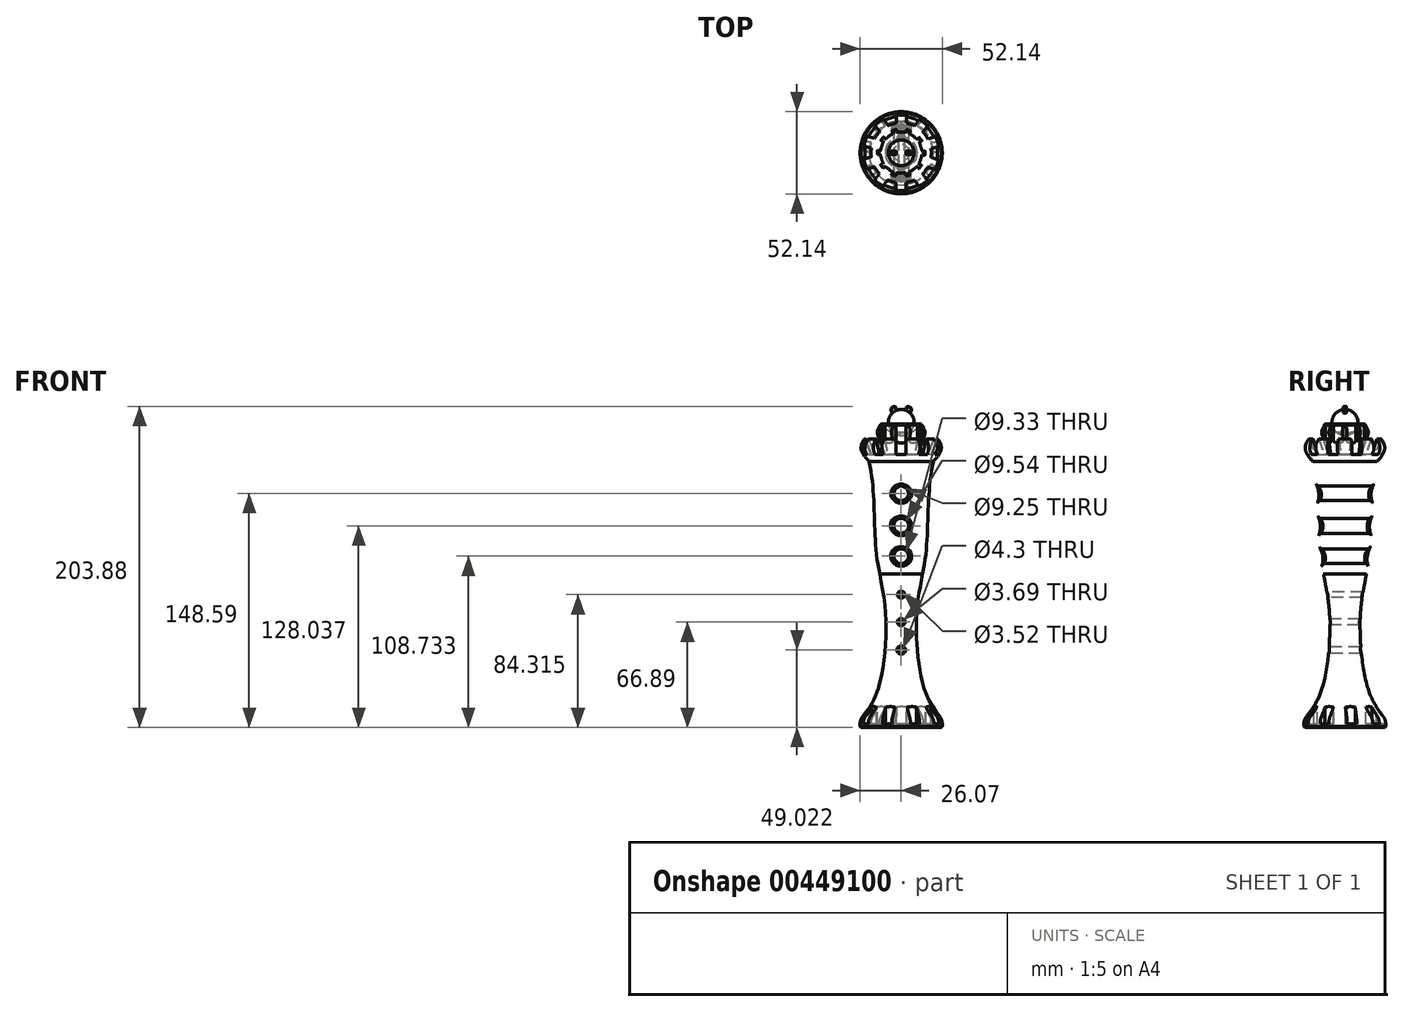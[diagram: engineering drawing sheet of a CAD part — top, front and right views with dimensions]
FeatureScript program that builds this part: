
annotation { "Feature Type Name" : "Feature", "Feature Type Description" : "" }
export const myFeature = defineFeature(function(context is Context, id is Id, definition is map)
    precondition{}
    {
        {
            var Q0;
            Q0=qCreatedBy(makeId("Front.planeOp"),FACE);
            var sketch = newSketch(context, id + "F0", { "sketchPlane" : qUnion([Q0])});
            skLineSegment(sketch, "E0", {"start": v(0, -66.9) * mm, "end": v(-25.47, -66.9) * mm});
            skLineSegment(sketch, "E1", {"start": v(-25.47, -66.9) * mm, "end": v(-26.07, -66.28) * mm});
            skLineSegment(sketch, "E2", {"start": v(-26.07, -66.28) * mm, "end": v(-26.07, -61.96) * mm});
            skFitSpline(sketch, "E3", {"points": [v(-26.07, -61.96) * mm, v(-14.8, -42.88) * mm, v(-9.75, 3.93) * mm, v(-13.6, 30.68) * mm], "startDerivative": vector(46.72, 58.33) * mm, "endDerivative": vector(-14.64, 88.37) * mm});
            skLineSegment(sketch, "E4", {"start": v(0, 71.96) * mm, "end": v(0, -66.9) * mm});
            skFitSpline(sketch, "E5", {"points": [v(-13.6, 30.68) * mm, v(-20.4, 102.06) * mm], "startDerivative": vector(-15.53, 69.23) * mm, "endDerivative": vector(-15.53, 69.23) * mm});
            skLineSegment(sketch, "E6", {"start": v(-20.4, 102.06) * mm, "end": v(0, 102.06) * mm});
            skLineSegment(sketch, "E7", {"start": v(0, 102.06) * mm, "end": v(0, 71.96) * mm});
            skFitSpline(sketch, "E8", {"points": [v(-20.4, 102.06) * mm, v(-23.45, 105.65) * mm, v(-25.43, 109.97) * mm, v(-23.1, 116.39) * mm], "startDerivative": vector(-17.16, 17.67) * mm, "endDerivative": vector(13.07, 17.45) * mm});
            skLineSegment(sketch, "E9", {"start": v(-23.1, 116.39) * mm, "end": v(-19.12, 106.54) * mm});
            skLineSegment(sketch, "E10", {"start": v(-19.12, 106.54) * mm, "end": v(0, 106.54) * mm});
            skLineSegment(sketch, "E11", {"start": v(0, 106.54) * mm, "end": v(0, 102.06) * mm});
            skLineSegment(sketch, "E12", {"start": v(0, 126.8) * mm, "end": v(0, 106.54) * mm});
            skLineSegment(sketch, "E13.MirrorCS", {"start": v(9.8, 106.54) * mm, "end": v(0, 106.54) * mm});
            skPoint(sketch, "E14.orphan", {"position": v(19.12, 106.54) * mm});
            skPoint(sketch, "E15", {"position": v(-3.48, 106.54) * mm});
            skFitSpline(sketch, "E16", {"points": [v(-10.2, 106.54) * mm, v(-14.51, 117.77) * mm, v(-15, 121.47) * mm, v(-13.02, 125.3) * mm], "startDerivative": vector(-11.04, 27.47) * mm, "endDerivative": vector(9.28, 14.07) * mm});
            skFitSpline(sketch, "E17", {"points": [v(-13.02, 125.3) * mm, v(-12.3, 125.9) * mm, v(-9.15, 122.08) * mm, v(0, 120.1) * mm], "startDerivative": vector(4.28, 6.55) * mm, "endDerivative": vector(21.3, -0.4) * mm});
            skLineSegment(sketch, "E18", {"start": v(0, 120.1) * mm, "end": v(0, 106.54) * mm});
            skCircle(sketch, "E19", {"center": v(0, 126.8) * mm, "radius": 8.23 * mm});
            skLineSegment(sketch, "E20", {"start": v(0, 137.4) * mm, "end": v(0, 116.67) * mm});
            skSolve(sketch);
        }
        {
            var Q0;
            {var subQ3=sQuery(id+"F0.wireOp",EDGE,"E0");Q0=makeQuery(id+"F0.imprint","IMPRINT",FACE,{"disambiguationData":[TD([[makeQuery(id+"F0.imprint","IMPRINT",EDGE,{"derivedFrom":subQ3}),-1.0]])]});}
            var Q1;
            Q1=makeQuery(id+"F0.imprint","IMPRINT",FACE,{"disambiguationData":[TD([[makeQuery(id+"F0.imprint","IMPRINT",EDGE,{"derivedFrom":sQuery(id+"F0.wireOp",EDGE,"E6")}),1.0]])]});
            var Q2;
            {var subQ2=sQuery(id+"F0.wireOp",EDGE,"E16");Q2=makeQuery(id+"F0.imprint","IMPRINT",FACE,{"disambiguationData":[TD([[makeQuery(id+"F0.imprint","IMPRINT",EDGE,{"derivedFrom":subQ2}),-1.0]])]});}
            var Q3;
            Q3=sQuery(id+"F0.wireOp",EDGE,"E4");
            revolve(context, id + "F1", {"entities" : qUnion([Q0, Q1, Q2]), "axis" : qUnion([Q3]), "revolveType" : RevolveType.FULL});
        }
        {
            var Q0;
            Q0=qCreatedBy(makeId("Top.planeOp"),FACE);
            var sketch = newSketch(context, id + "F2", { "sketchPlane" : qUnion([Q0])});
            skLineSegment(sketch, "E21.bottom", {"start": v(-3.06, 26.92) * mm, "end": v(3.2, 26.92) * mm});
            skLineSegment(sketch, "E21.top", {"start": v(-3.06, 19.93) * mm, "end": v(3.2, 19.93) * mm});
            skLineSegment(sketch, "E21.left", {"start": v(-3.06, 26.92) * mm, "end": v(-3.06, 19.93) * mm});
            skLineSegment(sketch, "E21.right", {"start": v(3.2, 26.92) * mm, "end": v(3.2, 19.93) * mm});
            skLineSegment(sketch, "E22.1.0", {"start": v(-14.84, 22.68) * mm, "end": v(-10.36, 17.33) * mm});
            skLineSegment(sketch, "E22.1.1", {"start": v(-19.65, 18.65) * mm, "end": v(-14.84, 22.68) * mm});
            skLineSegment(sketch, "E22.1.2", {"start": v(-19.65, 18.65) * mm, "end": v(-15.16, 13.3) * mm});
            skLineSegment(sketch, "E22.1.3", {"start": v(-15.16, 13.3) * mm, "end": v(-10.36, 17.33) * mm});
            skLineSegment(sketch, "E22.2.0", {"start": v(-25.95, 7.83) * mm, "end": v(-19.07, 6.62) * mm});
            skLineSegment(sketch, "E22.2.1", {"start": v(-27.04, 1.66) * mm, "end": v(-25.95, 7.83) * mm});
            skLineSegment(sketch, "E22.2.2", {"start": v(-27.04, 1.66) * mm, "end": v(-20.16, 0.45) * mm});
            skLineSegment(sketch, "E22.2.3", {"start": v(-20.16, 0.45) * mm, "end": v(-19.07, 6.62) * mm});
            skLineSegment(sketch, "E22.3.0", {"start": v(-24.91, -10.68) * mm, "end": v(-18.87, -7.19) * mm});
            skLineSegment(sketch, "E22.3.1", {"start": v(-21.78, -16.1) * mm, "end": v(-24.91, -10.68) * mm});
            skLineSegment(sketch, "E22.3.2", {"start": v(-21.78, -16.1) * mm, "end": v(-15.73, -12.62) * mm});
            skLineSegment(sketch, "E22.3.3", {"start": v(-15.73, -12.62) * mm, "end": v(-18.87, -7.19) * mm});
            skLineSegment(sketch, "E22.4.0", {"start": v(-12.22, -24.2) * mm, "end": v(-9.83, -17.63) * mm});
            skLineSegment(sketch, "E22.4.1", {"start": v(-6.33, -26.34) * mm, "end": v(-12.22, -24.2) * mm});
            skLineSegment(sketch, "E22.4.2", {"start": v(-6.33, -26.34) * mm, "end": v(-3.94, -19.78) * mm});
            skLineSegment(sketch, "E22.4.3", {"start": v(-3.94, -19.78) * mm, "end": v(-9.83, -17.63) * mm});
            skLineSegment(sketch, "E22.5.0", {"start": v(6.2, -26.4) * mm, "end": v(3.8, -19.83) * mm});
            skLineSegment(sketch, "E22.5.1", {"start": v(12.08, -24.25) * mm, "end": v(6.2, -26.4) * mm});
            skLineSegment(sketch, "E22.5.2", {"start": v(12.08, -24.25) * mm, "end": v(9.7, -17.68) * mm});
            skLineSegment(sketch, "E22.5.3", {"start": v(9.7, -17.68) * mm, "end": v(3.8, -19.83) * mm});
            skLineSegment(sketch, "E22.6.0", {"start": v(21.7, -16.24) * mm, "end": v(15.66, -12.75) * mm});
            skLineSegment(sketch, "E22.6.1", {"start": v(24.84, -10.8) * mm, "end": v(21.7, -16.24) * mm});
            skLineSegment(sketch, "E22.6.2", {"start": v(24.84, -10.8) * mm, "end": v(18.8, -7.32) * mm});
            skLineSegment(sketch, "E22.6.3", {"start": v(18.8, -7.32) * mm, "end": v(15.66, -12.75) * mm});
            skLineSegment(sketch, "E22.7.0", {"start": v(27.07, 1.51) * mm, "end": v(20.19, 0.3) * mm});
            skLineSegment(sketch, "E22.7.1", {"start": v(25.98, 7.69) * mm, "end": v(27.07, 1.51) * mm});
            skLineSegment(sketch, "E22.7.2", {"start": v(25.98, 7.69) * mm, "end": v(19.1, 6.48) * mm});
            skLineSegment(sketch, "E22.7.3", {"start": v(19.1, 6.48) * mm, "end": v(20.19, 0.3) * mm});
            skLineSegment(sketch, "E22.8.0", {"start": v(19.76, 18.56) * mm, "end": v(15.27, 13.2) * mm});
            skLineSegment(sketch, "E22.8.1", {"start": v(14.96, 22.59) * mm, "end": v(19.76, 18.56) * mm});
            skLineSegment(sketch, "E22.8.2", {"start": v(14.96, 22.59) * mm, "end": v(10.47, 17.24) * mm});
            skLineSegment(sketch, "E22.8.3", {"start": v(10.47, 17.24) * mm, "end": v(15.27, 13.2) * mm});
            skPoint(sketch, "E22.center", {"position": v(0, 0) * mm});
            skSolve(sketch);
        }
        {
            var Q0;
            Q0=qSketchRegion(id+"F2",true);
            extrude(context, id + "F3", {"entities" : qUnion([Q0]), "operationType" : NewBodyOperationType.REMOVE, "oppositeDirection" : true, "depth" : 64.73 * mm});
        }
        {
            var Q0;
            {var subQ0=sQuery(id+"F0.wireOp",EDGE,"E2");var subQ1=sQuery(id+"F0.wireOp",EDGE,"E3");Q0=makeQuery(id+"F3.boolean.opBoolean","SPLIT",EDGE,{"disambiguationData":[TD([makeQuery(id+"F3.opExtrude","SWEPT_FACE",FACE,{"disambiguationData":[OSD([sQuery(id+"F2.wireOp",EDGE,"E22.1.2")])]})])],"derivedFrom":makeQuery(id+"F1.opRevolve","SWEPT_EDGE",EDGE,{"disambiguationData":[OSD([subQ0,subQ1])]})});}
            var Q1;
            {var subQ0=sQuery(id+"F0.wireOp",EDGE,"E2");var subQ1=sQuery(id+"F0.wireOp",EDGE,"E3");Q1=makeQuery(id+"F3.boolean.opBoolean","SPLIT",EDGE,{"disambiguationData":[TD([makeQuery(id+"F3.opExtrude","SWEPT_FACE",FACE,{"disambiguationData":[OSD([sQuery(id+"F2.wireOp",EDGE,"E22.2.2")])]})])],"derivedFrom":makeQuery(id+"F1.opRevolve","SWEPT_EDGE",EDGE,{"disambiguationData":[OSD([subQ0,subQ1])]})});}
            var Q2;
            {var subQ0=sQuery(id+"F0.wireOp",EDGE,"E2");var subQ1=sQuery(id+"F0.wireOp",EDGE,"E3");Q2=makeQuery(id+"F3.boolean.opBoolean","SPLIT",EDGE,{"disambiguationData":[TD([makeQuery(id+"F3.opExtrude","SWEPT_FACE",FACE,{"disambiguationData":[OSD([sQuery(id+"F2.wireOp",EDGE,"E22.3.2")])]})])],"derivedFrom":makeQuery(id+"F1.opRevolve","SWEPT_EDGE",EDGE,{"disambiguationData":[OSD([subQ0,subQ1])]})});}
            var Q3;
            {var subQ0=sQuery(id+"F0.wireOp",EDGE,"E2");var subQ1=sQuery(id+"F0.wireOp",EDGE,"E3");Q3=makeQuery(id+"F3.boolean.opBoolean","SPLIT",EDGE,{"disambiguationData":[TD([makeQuery(id+"F3.opExtrude","SWEPT_FACE",FACE,{"disambiguationData":[OSD([sQuery(id+"F2.wireOp",EDGE,"E21.left")])]})])],"derivedFrom":makeQuery(id+"F1.opRevolve","SWEPT_EDGE",EDGE,{"disambiguationData":[OSD([subQ0,subQ1])]})});}
            var Q4;
            {var subQ0=sQuery(id+"F0.wireOp",EDGE,"E2");var subQ1=sQuery(id+"F0.wireOp",EDGE,"E3");Q4=makeQuery(id+"F3.boolean.opBoolean","SPLIT",EDGE,{"disambiguationData":[TD([makeQuery(id+"F3.opExtrude","SWEPT_FACE",FACE,{"disambiguationData":[OSD([sQuery(id+"F2.wireOp",EDGE,"E21.right")])]})])],"derivedFrom":makeQuery(id+"F1.opRevolve","SWEPT_EDGE",EDGE,{"disambiguationData":[OSD([subQ0,subQ1])]})});}
            var Q5;
            {var subQ0=sQuery(id+"F0.wireOp",EDGE,"E2");var subQ1=sQuery(id+"F0.wireOp",EDGE,"E3");Q5=makeQuery(id+"F3.boolean.opBoolean","SPLIT",EDGE,{"disambiguationData":[TD([makeQuery(id+"F3.opExtrude","SWEPT_FACE",FACE,{"disambiguationData":[OSD([sQuery(id+"F2.wireOp",EDGE,"E22.7.2")])]})])],"derivedFrom":makeQuery(id+"F1.opRevolve","SWEPT_EDGE",EDGE,{"disambiguationData":[OSD([subQ0,subQ1])]})});}
            var Q6;
            {var subQ0=sQuery(id+"F0.wireOp",EDGE,"E2");var subQ1=sQuery(id+"F0.wireOp",EDGE,"E3");Q6=makeQuery(id+"F3.boolean.opBoolean","SPLIT",EDGE,{"disambiguationData":[TD([makeQuery(id+"F3.opExtrude","SWEPT_FACE",FACE,{"disambiguationData":[OSD([sQuery(id+"F2.wireOp",EDGE,"E22.6.2")])]})])],"derivedFrom":makeQuery(id+"F1.opRevolve","SWEPT_EDGE",EDGE,{"disambiguationData":[OSD([subQ0,subQ1])]})});}
            var Q7;
            {var subQ0=sQuery(id+"F0.wireOp",EDGE,"E2");var subQ1=sQuery(id+"F0.wireOp",EDGE,"E3");Q7=makeQuery(id+"F3.boolean.opBoolean","SPLIT",EDGE,{"disambiguationData":[TD([makeQuery(id+"F3.opExtrude","SWEPT_FACE",FACE,{"disambiguationData":[OSD([sQuery(id+"F2.wireOp",EDGE,"E22.5.2")])]})])],"derivedFrom":makeQuery(id+"F1.opRevolve","SWEPT_EDGE",EDGE,{"disambiguationData":[OSD([subQ0,subQ1])]})});}
            var Q8;
            {var subQ0=sQuery(id+"F0.wireOp",EDGE,"E2");var subQ1=sQuery(id+"F0.wireOp",EDGE,"E3");Q8=makeQuery(id+"F3.boolean.opBoolean","SPLIT",EDGE,{"disambiguationData":[TD([makeQuery(id+"F3.opExtrude","SWEPT_FACE",FACE,{"disambiguationData":[OSD([sQuery(id+"F2.wireOp",EDGE,"E22.4.2")])]})])],"derivedFrom":makeQuery(id+"F1.opRevolve","SWEPT_EDGE",EDGE,{"disambiguationData":[OSD([subQ0,subQ1])]})});}
            fillet(context, id + "F4", {"entities" : qUnion([Q0, Q1, Q2, Q3, Q4, Q5, Q6, Q7, Q8]), "radius" : 7.18 * mm, "tangentPropagation" : true, "allowEdgeOverflow" : false});
        }
        {
            var Q0;
            Q0=qCreatedBy(makeId("Front.planeOp"),FACE);
            var sketch = newSketch(context, id + "F5", { "sketchPlane" : qUnion([Q0])});
            skCircle(sketch, "E23", {"center": v(0, 81.7) * mm, "radius": 4.62 * mm});
            skCircle(sketch, "E24", {"center": v(0, 61.15) * mm, "radius": 4.77 * mm});
            skCircle(sketch, "E25", {"center": v(0, 41.84) * mm, "radius": 4.67 * mm});
            skCircle(sketch, "E26", {"center": v(0, 17.43) * mm, "radius": 1.76 * mm});
            skCircle(sketch, "E27", {"center": v(0, 0) * mm, "radius": 1.84 * mm});
            skCircle(sketch, "E28", {"center": v(0, -17.87) * mm, "radius": 2.15 * mm});
            skLineSegment(sketch, "E29", {"start": v(0, 92.72) * mm, "end": v(0, -43.86) * mm});
            skSolve(sketch);
        }
        {
            var Q0;
            Q0=qSketchRegion(id+"F5",true);
            extrude(context, id + "F6", {"entities" : qUnion([Q0]), "operationType" : NewBodyOperationType.REMOVE, "endBound" : BoundingType.SYMMETRIC, "oppositeDirection" : true, "depth" : 127 * mm});
        }
        {
            var Q0;
            {var subQ0=sQuery(id+"F0.wireOp",EDGE,"E3");Q0=makeQuery(id+"F6.boolean.opBoolean","INTERSECT",EDGE,{"disambiguationData":[OD(1.0)],"derivedFrom":[makeQuery(id+"F1.opRevolve","SWEPT_FACE",FACE,{"disambiguationData":[OSD([subQ0]),TDD([makeQuery(id+"F0.imprint","IMPRINT",EDGE,{"disambiguationData":[TD([[makeQuery(id+"F0.imprint","INTERSECT",VERTEX,{"derivedFrom":[sQuery(id+"F0.wireOp",EDGE,"E2"),subQ0]}),-1.0]])],"derivedFrom":subQ0})])]}),makeQuery(id+"F6.opExtrude","SWEPT_FACE",FACE,{"disambiguationData":[OSD([sQuery(id+"F5.wireOp",EDGE,"E23")])]})]});}
            var Q1;
            {var subQ0=sQuery(id+"F0.wireOp",EDGE,"E3");Q1=makeQuery(id+"F6.boolean.opBoolean","INTERSECT",EDGE,{"disambiguationData":[OD(1.0)],"derivedFrom":[makeQuery(id+"F1.opRevolve","SWEPT_FACE",FACE,{"disambiguationData":[OSD([subQ0]),TDD([makeQuery(id+"F0.imprint","IMPRINT",EDGE,{"disambiguationData":[TD([[makeQuery(id+"F0.imprint","INTERSECT",VERTEX,{"derivedFrom":[sQuery(id+"F0.wireOp",EDGE,"E2"),subQ0]}),-1.0]])],"derivedFrom":subQ0})])]}),makeQuery(id+"F6.opExtrude","SWEPT_FACE",FACE,{"disambiguationData":[OSD([sQuery(id+"F5.wireOp",EDGE,"E24")])]})]});}
            var Q2;
            {var subQ0=sQuery(id+"F0.wireOp",EDGE,"E3");Q2=makeQuery(id+"F6.boolean.opBoolean","INTERSECT",EDGE,{"disambiguationData":[OD(1.0)],"derivedFrom":[makeQuery(id+"F1.opRevolve","SWEPT_FACE",FACE,{"disambiguationData":[OSD([subQ0]),TDD([makeQuery(id+"F0.imprint","IMPRINT",EDGE,{"disambiguationData":[TD([[makeQuery(id+"F0.imprint","INTERSECT",VERTEX,{"derivedFrom":[sQuery(id+"F0.wireOp",EDGE,"E2"),subQ0]}),-1.0]])],"derivedFrom":subQ0})])]}),makeQuery(id+"F6.opExtrude","SWEPT_FACE",FACE,{"disambiguationData":[OSD([sQuery(id+"F5.wireOp",EDGE,"450bc9a7-5f52-43cc-974d-208ef459b1f0")])]})]});}
            var Q3;
            {var subQ0=sQuery(id+"F0.wireOp",EDGE,"E3");Q3=makeQuery(id+"F6.boolean.opBoolean","INTERSECT",EDGE,{"disambiguationData":[OD(1.0)],"derivedFrom":[makeQuery(id+"F1.opRevolve","SWEPT_FACE",FACE,{"disambiguationData":[OSD([subQ0]),TDD([makeQuery(id+"F0.imprint","IMPRINT",EDGE,{"disambiguationData":[TD([[makeQuery(id+"F0.imprint","INTERSECT",VERTEX,{"derivedFrom":[sQuery(id+"F0.wireOp",EDGE,"E2"),subQ0]}),-1.0]])],"derivedFrom":subQ0})])]}),makeQuery(id+"F6.opExtrude","SWEPT_FACE",FACE,{"disambiguationData":[OSD([sQuery(id+"F5.wireOp",EDGE,"E25")])]})]});}
            var Q4;
            {var subQ0=sQuery(id+"F0.wireOp",EDGE,"E3");Q4=makeQuery(id+"F6.boolean.opBoolean","INTERSECT",EDGE,{"disambiguationData":[OD(1.0)],"derivedFrom":[makeQuery(id+"F1.opRevolve","SWEPT_FACE",FACE,{"disambiguationData":[OSD([subQ0]),TDD([makeQuery(id+"F0.imprint","IMPRINT",EDGE,{"disambiguationData":[TD([[makeQuery(id+"F0.imprint","INTERSECT",VERTEX,{"derivedFrom":[sQuery(id+"F0.wireOp",EDGE,"E2"),subQ0]}),-1.0]])],"derivedFrom":subQ0})])]}),makeQuery(id+"F6.opExtrude","SWEPT_FACE",FACE,{"disambiguationData":[OSD([sQuery(id+"F5.wireOp",EDGE,"E26")])]})]});}
            var Q5;
            {var subQ0=sQuery(id+"F0.wireOp",EDGE,"E3");Q5=makeQuery(id+"F6.boolean.opBoolean","INTERSECT",EDGE,{"disambiguationData":[OD(1.0)],"derivedFrom":[makeQuery(id+"F1.opRevolve","SWEPT_FACE",FACE,{"disambiguationData":[OSD([subQ0]),TDD([makeQuery(id+"F0.imprint","IMPRINT",EDGE,{"disambiguationData":[TD([[makeQuery(id+"F0.imprint","INTERSECT",VERTEX,{"derivedFrom":[sQuery(id+"F0.wireOp",EDGE,"E2"),subQ0]}),-1.0]])],"derivedFrom":subQ0})])]}),makeQuery(id+"F6.opExtrude","SWEPT_FACE",FACE,{"disambiguationData":[OSD([sQuery(id+"F5.wireOp",EDGE,"E27")])]})]});}
            var Q6;
            {var subQ0=sQuery(id+"F0.wireOp",EDGE,"E3");Q6=makeQuery(id+"F6.boolean.opBoolean","INTERSECT",EDGE,{"disambiguationData":[OD(1.0)],"derivedFrom":[makeQuery(id+"F1.opRevolve","SWEPT_FACE",FACE,{"disambiguationData":[OSD([subQ0]),TDD([makeQuery(id+"F0.imprint","IMPRINT",EDGE,{"disambiguationData":[TD([[makeQuery(id+"F0.imprint","INTERSECT",VERTEX,{"derivedFrom":[sQuery(id+"F0.wireOp",EDGE,"E2"),subQ0]}),-1.0]])],"derivedFrom":subQ0})])]}),makeQuery(id+"F6.opExtrude","SWEPT_FACE",FACE,{"disambiguationData":[OSD([sQuery(id+"F5.wireOp",EDGE,"E28")])]})]});}
            var Q7;
            {var subQ0=sQuery(id+"F0.wireOp",EDGE,"E3");Q7=makeQuery(id+"F6.boolean.opBoolean","INTERSECT",EDGE,{"disambiguationData":[OD(0.0)],"derivedFrom":[makeQuery(id+"F1.opRevolve","SWEPT_FACE",FACE,{"disambiguationData":[OSD([subQ0]),TDD([makeQuery(id+"F0.imprint","IMPRINT",EDGE,{"disambiguationData":[TD([[makeQuery(id+"F0.imprint","INTERSECT",VERTEX,{"derivedFrom":[sQuery(id+"F0.wireOp",EDGE,"E2"),subQ0]}),-1.0]])],"derivedFrom":subQ0})])]}),makeQuery(id+"F6.opExtrude","SWEPT_FACE",FACE,{"disambiguationData":[OSD([sQuery(id+"F5.wireOp",EDGE,"E23")])]})]});}
            var Q8;
            {var subQ0=sQuery(id+"F0.wireOp",EDGE,"E3");Q8=makeQuery(id+"F6.boolean.opBoolean","INTERSECT",EDGE,{"disambiguationData":[OD(0.0)],"derivedFrom":[makeQuery(id+"F1.opRevolve","SWEPT_FACE",FACE,{"disambiguationData":[OSD([subQ0]),TDD([makeQuery(id+"F0.imprint","IMPRINT",EDGE,{"disambiguationData":[TD([[makeQuery(id+"F0.imprint","INTERSECT",VERTEX,{"derivedFrom":[sQuery(id+"F0.wireOp",EDGE,"E2"),subQ0]}),-1.0]])],"derivedFrom":subQ0})])]}),makeQuery(id+"F6.opExtrude","SWEPT_FACE",FACE,{"disambiguationData":[OSD([sQuery(id+"F5.wireOp",EDGE,"E24")])]})]});}
            var Q9;
            {var subQ0=sQuery(id+"F0.wireOp",EDGE,"E3");Q9=makeQuery(id+"F6.boolean.opBoolean","INTERSECT",EDGE,{"disambiguationData":[OD(0.0)],"derivedFrom":[makeQuery(id+"F1.opRevolve","SWEPT_FACE",FACE,{"disambiguationData":[OSD([subQ0]),TDD([makeQuery(id+"F0.imprint","IMPRINT",EDGE,{"disambiguationData":[TD([[makeQuery(id+"F0.imprint","INTERSECT",VERTEX,{"derivedFrom":[sQuery(id+"F0.wireOp",EDGE,"E2"),subQ0]}),-1.0]])],"derivedFrom":subQ0})])]}),makeQuery(id+"F6.opExtrude","SWEPT_FACE",FACE,{"disambiguationData":[OSD([sQuery(id+"F5.wireOp",EDGE,"450bc9a7-5f52-43cc-974d-208ef459b1f0")])]})]});}
            var Q10;
            {var subQ0=sQuery(id+"F0.wireOp",EDGE,"E3");Q10=makeQuery(id+"F6.boolean.opBoolean","INTERSECT",EDGE,{"disambiguationData":[OD(0.0)],"derivedFrom":[makeQuery(id+"F1.opRevolve","SWEPT_FACE",FACE,{"disambiguationData":[OSD([subQ0]),TDD([makeQuery(id+"F0.imprint","IMPRINT",EDGE,{"disambiguationData":[TD([[makeQuery(id+"F0.imprint","INTERSECT",VERTEX,{"derivedFrom":[sQuery(id+"F0.wireOp",EDGE,"E2"),subQ0]}),-1.0]])],"derivedFrom":subQ0})])]}),makeQuery(id+"F6.opExtrude","SWEPT_FACE",FACE,{"disambiguationData":[OSD([sQuery(id+"F5.wireOp",EDGE,"E25")])]})]});}
            var Q11;
            {var subQ0=sQuery(id+"F0.wireOp",EDGE,"E3");Q11=makeQuery(id+"F6.boolean.opBoolean","INTERSECT",EDGE,{"disambiguationData":[OD(0.0)],"derivedFrom":[makeQuery(id+"F1.opRevolve","SWEPT_FACE",FACE,{"disambiguationData":[OSD([subQ0]),TDD([makeQuery(id+"F0.imprint","IMPRINT",EDGE,{"disambiguationData":[TD([[makeQuery(id+"F0.imprint","INTERSECT",VERTEX,{"derivedFrom":[sQuery(id+"F0.wireOp",EDGE,"E2"),subQ0]}),-1.0]])],"derivedFrom":subQ0})])]}),makeQuery(id+"F6.opExtrude","SWEPT_FACE",FACE,{"disambiguationData":[OSD([sQuery(id+"F5.wireOp",EDGE,"E26")])]})]});}
            var Q12;
            {var subQ0=sQuery(id+"F0.wireOp",EDGE,"E3");Q12=makeQuery(id+"F6.boolean.opBoolean","INTERSECT",EDGE,{"disambiguationData":[OD(0.0)],"derivedFrom":[makeQuery(id+"F1.opRevolve","SWEPT_FACE",FACE,{"disambiguationData":[OSD([subQ0]),TDD([makeQuery(id+"F0.imprint","IMPRINT",EDGE,{"disambiguationData":[TD([[makeQuery(id+"F0.imprint","INTERSECT",VERTEX,{"derivedFrom":[sQuery(id+"F0.wireOp",EDGE,"E2"),subQ0]}),-1.0]])],"derivedFrom":subQ0})])]}),makeQuery(id+"F6.opExtrude","SWEPT_FACE",FACE,{"disambiguationData":[OSD([sQuery(id+"F5.wireOp",EDGE,"E27")])]})]});}
            var Q13;
            {var subQ0=sQuery(id+"F0.wireOp",EDGE,"E3");Q13=makeQuery(id+"F6.boolean.opBoolean","INTERSECT",EDGE,{"disambiguationData":[OD(0.0)],"derivedFrom":[makeQuery(id+"F1.opRevolve","SWEPT_FACE",FACE,{"disambiguationData":[OSD([subQ0]),TDD([makeQuery(id+"F0.imprint","IMPRINT",EDGE,{"disambiguationData":[TD([[makeQuery(id+"F0.imprint","INTERSECT",VERTEX,{"derivedFrom":[sQuery(id+"F0.wireOp",EDGE,"E2"),subQ0]}),-1.0]])],"derivedFrom":subQ0})])]}),makeQuery(id+"F6.opExtrude","SWEPT_FACE",FACE,{"disambiguationData":[OSD([sQuery(id+"F5.wireOp",EDGE,"E28")])]})]});}
            fillet(context, id + "F7", {"entities" : qUnion([Q0, Q1, Q2, Q3, Q4, Q5, Q6, Q7, Q8, Q9, Q10, Q11, Q12, Q13]), "radius" : 0.48 * mm, "tangentPropagation" : true, "allowEdgeOverflow" : false});
        }
        {
            var Q0;
            Q0=makeQuery(id+"F6.boolean.opBoolean","INTERSECT",EDGE,{"disambiguationData":[OD(0.0)],"derivedFrom":[makeQuery(id+"F1.opRevolve","SWEPT_FACE",FACE,{"disambiguationData":[OSD([sQuery(id+"F0.wireOp",EDGE,"E5")])]}),makeQuery(id+"F6.opExtrude","SWEPT_FACE",FACE,{"disambiguationData":[OSD([sQuery(id+"F5.wireOp",EDGE,"E25")])]})]});
            var Q1;
            Q1=makeQuery(id+"F6.boolean.opBoolean","INTERSECT",EDGE,{"disambiguationData":[OD(0.0)],"derivedFrom":[makeQuery(id+"F1.opRevolve","SWEPT_FACE",FACE,{"disambiguationData":[OSD([sQuery(id+"F0.wireOp",EDGE,"E5")])]}),makeQuery(id+"F6.opExtrude","SWEPT_FACE",FACE,{"disambiguationData":[OSD([sQuery(id+"F5.wireOp",EDGE,"450bc9a7-5f52-43cc-974d-208ef459b1f0")])]})]});
            var Q2;
            Q2=makeQuery(id+"F6.boolean.opBoolean","INTERSECT",EDGE,{"disambiguationData":[OD(0.0)],"derivedFrom":[makeQuery(id+"F1.opRevolve","SWEPT_FACE",FACE,{"disambiguationData":[OSD([sQuery(id+"F0.wireOp",EDGE,"E5")])]}),makeQuery(id+"F6.opExtrude","SWEPT_FACE",FACE,{"disambiguationData":[OSD([sQuery(id+"F5.wireOp",EDGE,"E24")])]})]});
            var Q3;
            Q3=makeQuery(id+"F6.boolean.opBoolean","INTERSECT",EDGE,{"disambiguationData":[OD(0.0)],"derivedFrom":[makeQuery(id+"F1.opRevolve","SWEPT_FACE",FACE,{"disambiguationData":[OSD([sQuery(id+"F0.wireOp",EDGE,"E5")])]}),makeQuery(id+"F6.opExtrude","SWEPT_FACE",FACE,{"disambiguationData":[OSD([sQuery(id+"F5.wireOp",EDGE,"E23")])]})]});
            var Q4;
            Q4=makeQuery(id+"F6.boolean.opBoolean","INTERSECT",EDGE,{"disambiguationData":[OD(1.0)],"derivedFrom":[makeQuery(id+"F1.opRevolve","SWEPT_FACE",FACE,{"disambiguationData":[OSD([sQuery(id+"F0.wireOp",EDGE,"E5")])]}),makeQuery(id+"F6.opExtrude","SWEPT_FACE",FACE,{"disambiguationData":[OSD([sQuery(id+"F5.wireOp",EDGE,"E25")])]})]});
            var Q5;
            Q5=makeQuery(id+"F6.boolean.opBoolean","INTERSECT",EDGE,{"disambiguationData":[OD(1.0)],"derivedFrom":[makeQuery(id+"F1.opRevolve","SWEPT_FACE",FACE,{"disambiguationData":[OSD([sQuery(id+"F0.wireOp",EDGE,"E5")])]}),makeQuery(id+"F6.opExtrude","SWEPT_FACE",FACE,{"disambiguationData":[OSD([sQuery(id+"F5.wireOp",EDGE,"450bc9a7-5f52-43cc-974d-208ef459b1f0")])]})]});
            var Q6;
            Q6=makeQuery(id+"F6.boolean.opBoolean","INTERSECT",EDGE,{"disambiguationData":[OD(1.0)],"derivedFrom":[makeQuery(id+"F1.opRevolve","SWEPT_FACE",FACE,{"disambiguationData":[OSD([sQuery(id+"F0.wireOp",EDGE,"E5")])]}),makeQuery(id+"F6.opExtrude","SWEPT_FACE",FACE,{"disambiguationData":[OSD([sQuery(id+"F5.wireOp",EDGE,"E24")])]})]});
            var Q7;
            Q7=makeQuery(id+"F6.boolean.opBoolean","INTERSECT",EDGE,{"disambiguationData":[OD(1.0)],"derivedFrom":[makeQuery(id+"F1.opRevolve","SWEPT_FACE",FACE,{"disambiguationData":[OSD([sQuery(id+"F0.wireOp",EDGE,"E5")])]}),makeQuery(id+"F6.opExtrude","SWEPT_FACE",FACE,{"disambiguationData":[OSD([sQuery(id+"F5.wireOp",EDGE,"E23")])]})]});
            fillet(context, id + "F8", {"entities" : qUnion([Q0, Q1, Q2, Q3, Q4, Q5, Q6, Q7]), "radius" : 1.43 * mm, "tangentPropagation" : true, "allowEdgeOverflow" : false});
        }
        {
            var Q0;
            Q0=sQuery(id+"F0.wireOp",VERTEX,"E15");
            var Q1;
            Q1=qCreatedBy(makeId("Top.planeOp"),FACE);
            cPlane(context, id + "F9", {"entities" : qUnion([Q0, Q1]), "cplaneType" : CPlaneType.PLANE_POINT, "offset" : 25.4 * mm, "width" : 152.4 * mm, "height" : 152.4 * mm});
        }
        {
            var Q0;
            Q0=qCreatedBy(id+"F9.planeOp",FACE);
            var sketch = newSketch(context, id + "F10", { "sketchPlane" : qUnion([Q0])});
            skLineSegment(sketch, "E30.bottom", {"start": v(-3.12, 27.97) * mm, "end": v(3.44, 27.97) * mm});
            skLineSegment(sketch, "E30.top", {"start": v(-3.12, 13.02) * mm, "end": v(3.44, 13.02) * mm});
            skLineSegment(sketch, "E30.left", {"start": v(-3.12, 27.97) * mm, "end": v(-3.12, 13.02) * mm});
            skLineSegment(sketch, "E30.right", {"start": v(3.44, 27.97) * mm, "end": v(3.44, 13.02) * mm});
            skLineSegment(sketch, "E31.1.0", {"start": v(-18.96, 20.8) * mm, "end": v(-10.17, 8.7) * mm});
            skLineSegment(sketch, "E31.1.1", {"start": v(-10.17, 8.7) * mm, "end": v(-4.87, 12.55) * mm});
            skLineSegment(sketch, "E31.1.2", {"start": v(-13.66, 24.65) * mm, "end": v(-4.87, 12.55) * mm});
            skLineSegment(sketch, "E31.1.3", {"start": v(-18.96, 20.8) * mm, "end": v(-13.66, 24.65) * mm});
            skLineSegment(sketch, "E31.2.0", {"start": v(-27.56, 5.68) * mm, "end": v(-13.34, 1.06) * mm});
            skLineSegment(sketch, "E31.2.1", {"start": v(-13.34, 1.06) * mm, "end": v(-11.32, 7.3) * mm});
            skLineSegment(sketch, "E31.2.2", {"start": v(-25.54, 11.91) * mm, "end": v(-11.32, 7.3) * mm});
            skLineSegment(sketch, "E31.2.3", {"start": v(-27.56, 5.68) * mm, "end": v(-25.54, 11.91) * mm});
            skLineSegment(sketch, "E31.3.0", {"start": v(-25.64, -11.6) * mm, "end": v(-11.42, -6.99) * mm});
            skLineSegment(sketch, "E31.3.1", {"start": v(-11.42, -6.99) * mm, "end": v(-13.44, -0.75) * mm});
            skLineSegment(sketch, "E31.3.2", {"start": v(-27.66, -5.37) * mm, "end": v(-13.44, -0.75) * mm});
            skLineSegment(sketch, "E31.3.3", {"start": v(-25.64, -11.6) * mm, "end": v(-27.66, -5.37) * mm});
            skLineSegment(sketch, "E31.4.0", {"start": v(-13.92, -24.46) * mm, "end": v(-5.13, -12.36) * mm});
            skLineSegment(sketch, "E31.4.1", {"start": v(-5.13, -12.36) * mm, "end": v(-10.43, -8.51) * mm});
            skLineSegment(sketch, "E31.4.2", {"start": v(-19.22, -20.6) * mm, "end": v(-10.43, -8.51) * mm});
            skLineSegment(sketch, "E31.4.3", {"start": v(-13.92, -24.46) * mm, "end": v(-19.22, -20.6) * mm});
            skLineSegment(sketch, "E31.5.0", {"start": v(3.12, -27.97) * mm, "end": v(3.12, -13.02) * mm});
            skLineSegment(sketch, "E31.5.1", {"start": v(3.12, -13.02) * mm, "end": v(-3.44, -13.02) * mm});
            skLineSegment(sketch, "E31.5.2", {"start": v(-3.44, -27.97) * mm, "end": v(-3.44, -13.02) * mm});
            skLineSegment(sketch, "E31.5.3", {"start": v(3.12, -27.97) * mm, "end": v(-3.44, -27.97) * mm});
            skLineSegment(sketch, "E31.6.0", {"start": v(18.96, -20.8) * mm, "end": v(10.17, -8.7) * mm});
            skLineSegment(sketch, "E31.6.1", {"start": v(10.17, -8.7) * mm, "end": v(4.87, -12.55) * mm});
            skLineSegment(sketch, "E31.6.2", {"start": v(13.66, -24.65) * mm, "end": v(4.87, -12.55) * mm});
            skLineSegment(sketch, "E31.6.3", {"start": v(18.96, -20.8) * mm, "end": v(13.66, -24.65) * mm});
            skLineSegment(sketch, "E31.7.0", {"start": v(27.56, -5.68) * mm, "end": v(13.34, -1.06) * mm});
            skLineSegment(sketch, "E31.7.1", {"start": v(13.34, -1.06) * mm, "end": v(11.32, -7.3) * mm});
            skLineSegment(sketch, "E31.7.2", {"start": v(25.54, -11.91) * mm, "end": v(11.32, -7.3) * mm});
            skLineSegment(sketch, "E31.7.3", {"start": v(27.56, -5.68) * mm, "end": v(25.54, -11.91) * mm});
            skLineSegment(sketch, "E31.8.0", {"start": v(25.64, 11.6) * mm, "end": v(11.42, 6.99) * mm});
            skLineSegment(sketch, "E31.8.1", {"start": v(11.42, 6.99) * mm, "end": v(13.44, 0.75) * mm});
            skLineSegment(sketch, "E31.8.2", {"start": v(27.66, 5.37) * mm, "end": v(13.44, 0.75) * mm});
            skLineSegment(sketch, "E31.8.3", {"start": v(25.64, 11.6) * mm, "end": v(27.66, 5.37) * mm});
            skLineSegment(sketch, "E31.9.0", {"start": v(13.92, 24.46) * mm, "end": v(5.13, 12.36) * mm});
            skLineSegment(sketch, "E31.9.1", {"start": v(5.13, 12.36) * mm, "end": v(10.43, 8.51) * mm});
            skLineSegment(sketch, "E31.9.2", {"start": v(19.22, 20.6) * mm, "end": v(10.43, 8.51) * mm});
            skLineSegment(sketch, "E31.9.3", {"start": v(13.92, 24.46) * mm, "end": v(19.22, 20.6) * mm});
            skPoint(sketch, "E31.center", {"position": v(0, 0) * mm});
            skSolve(sketch);
        }
        {
            var Q0;
            Q0 = qSketchRegion(id + "F10", true);
            extrude(context, id + "F11", {"entities" : qUnion([Q0]), "operationType" : NewBodyOperationType.REMOVE, "depth" : 25.4 * mm});
        }
        {
            var Q0;
            {var subQ0=sQuery(id+"F0.wireOp",EDGE,"E20");var subQ6=makeQuery(id+"F0.imprint","IMPRINT",VERTEX,{"derivedFrom":subQ0});Q0=makeQuery(id+"F0.imprint","IMPRINT",FACE,{"disambiguationData":[TD([[makeQuery(id+"F0.imprint","IMPRINT",EDGE,{"disambiguationData":[TD([[subQ6,1.0]])],"derivedFrom":subQ0}),-1.0]])]});}
            var Q1;
            Q1=sQuery(id+"F0.wireOp",EDGE,"E20");
            revolve(context, id + "F12", {"operationType" : NewBodyOperationType.ADD, "entities" : qUnion([Q0]), "axis" : qUnion([Q1]), "revolveType" : RevolveType.FULL});
        }
        {
            var Q0;
            Q0=qCreatedBy(makeId("Front.planeOp"),FACE);
            var sketch = newSketch(context, id + "F13", { "sketchPlane" : qUnion([Q0])});
            skFitSpline(sketch, "E32", {"points": [v(-4.82, 132.5) * mm, v(-5.6, 132.67) * mm, v(-6.34, 133.73) * mm, v(-6.58, 134.83) * mm, v(-6.23, 135.84) * mm, v(-5.45, 136.67) * mm, v(-4.31, 136.99) * mm, v(-3.44, 136.63) * mm, v(-3.1, 135.69) * mm, v(-2.98, 134.98) * mm, v(-2.86, 134.22) * mm], "startDerivative": vector(0, -15.22) * mm, "endDerivative": vector(1.3, -8.18) * mm});
            skLineSegment(sketch, "E33", {"start": v(-4.82, 132.5) * mm, "end": v(-2.86, 134.22) * mm});
            skFitSpline(sketch, "E34.MirrorCS", {"points": [v(4.82, 132.5) * mm, v(5.6, 132.67) * mm, v(6.34, 133.73) * mm, v(6.58, 134.83) * mm, v(6.23, 135.84) * mm, v(5.45, 136.67) * mm, v(4.31, 136.99) * mm, v(3.44, 136.63) * mm, v(3.1, 135.69) * mm, v(2.98, 134.98) * mm, v(2.86, 134.22) * mm], "startDerivative": vector(0, -15.22) * mm, "endDerivative": vector(-1.3, -8.18) * mm});
            skLineSegment(sketch, "E35", {"start": v(2.86, 134.22) * mm, "end": v(4.82, 132.5) * mm});
            skSolve(sketch);
        }
        {
            var Q0;
            Q0 = qSketchRegion(id + "F13", true);
            extrude(context, id + "F14", {"entities" : qUnion([Q0]), "operationType" : NewBodyOperationType.ADD, "endBound" : BoundingType.SYMMETRIC, "depth" : 2.03 * mm});
        }
        {
            var Q0;
            Q0=makeQuery(id+"F14.opExtrude","CAP_EDGE",EDGE,{"disambiguationData":[OSD([sQuery(id+"F13.wireOp",EDGE,"E32")])],"isStart":false});
            var Q1;
            Q1=makeQuery(id+"F14.opExtrude","CAP_EDGE",EDGE,{"disambiguationData":[OSD([sQuery(id+"F13.wireOp",EDGE,"E32")])],"isStart":true});
            var Q2;
            Q2=makeQuery(id+"F14.opExtrude","CAP_EDGE",EDGE,{"disambiguationData":[OSD([sQuery(id+"F13.wireOp",EDGE,"E34.MirrorCS")])],"isStart":false});
            var Q3;
            Q3=makeQuery(id+"F14.opExtrude","CAP_EDGE",EDGE,{"disambiguationData":[OSD([sQuery(id+"F13.wireOp",EDGE,"E34.MirrorCS")])],"isStart":true});
            fillet(context, id + "F15", {"entities" : qUnion([Q0, Q1, Q2, Q3]), "radius" : 0.43 * mm, "tangentPropagation" : true, "allowEdgeOverflow" : false});
        }
    });
